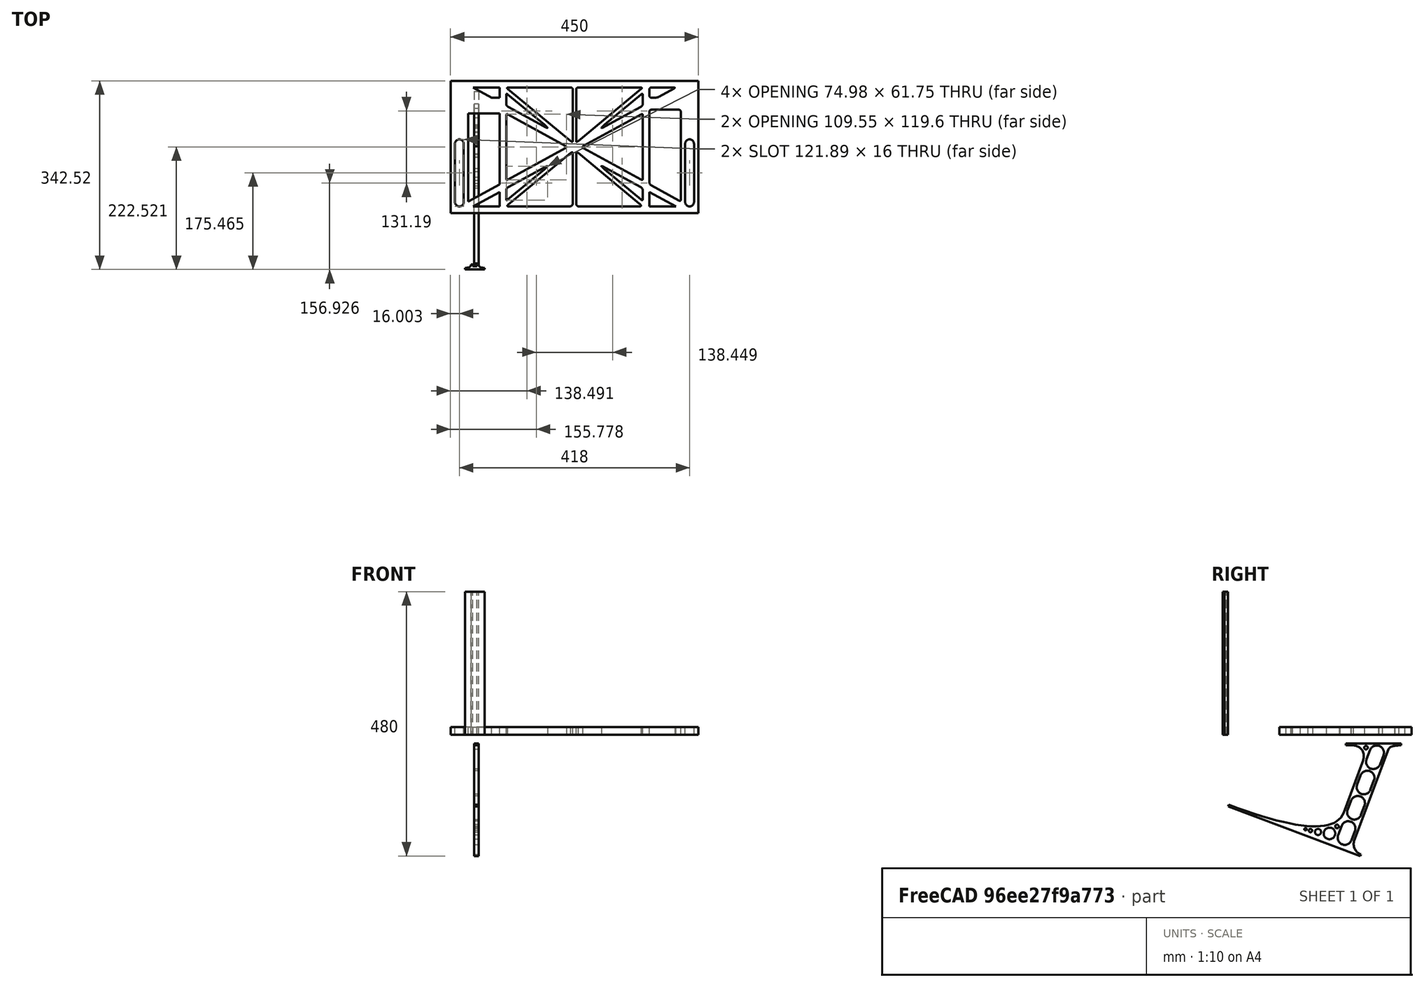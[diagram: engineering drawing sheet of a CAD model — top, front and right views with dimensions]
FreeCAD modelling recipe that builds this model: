
FCSTD DOCUMENT  (FreeCAD 0.19R0.19.2)
Label: laptopStand109
License: All rights reserved
LicenseURL: http://en.wikipedia.org/wiki/All_rights_reserved
objects: Sketcher::SketchObject×3, Part::Extrusion×3
note: 6 computed .brp shape members not serialized (recipe doc carries the construction recipe); baked Part::Feature solids carry a one-line shape summary decoded from their .brp

FEATURE [Sketcher::SketchObject] Sketch
  FullyConstrained = false
  sketch-geometry (298):
    g0: LineSegment StartX=-10.9272 StartY=-82.7794 StartZ=0 EndX=46.0728 EndY=-51.4823 EndZ=0
    g1: LineSegment StartX=366.073 StartY=-91.7794 StartZ=0 EndX=318.073 EndY=-65.424 EndZ=0
    g2: LineSegment StartX=-10.9272 StartY=77.3346 StartZ=0 EndX=-10.9272 EndY=-82.7794 EndZ=0
    g3: LineSegment StartX=-1.92719 StartY=-91.7794 StartZ=0 EndX=46.0728 EndY=-91.7794 EndZ=0
    g4: LineSegment StartX=318.073 StartY=-65.424 StartZ=0 EndX=318.073 EndY=-91.7794 EndZ=0
    g5: LineSegment StartX=318.073 StartY=-91.7794 StartZ=0 EndX=366.073 EndY=-91.7794 EndZ=0
    g6: LineSegment StartX=46.0728 StartY=-65.424 StartZ=0 EndX=-1.92719 EndY=-91.7794 EndZ=0
    g7: LineSegment StartX=46.0728 StartY=-65.424 StartZ=0 EndX=46.0728 EndY=-91.7794 EndZ=0
    g8: LineSegment StartX=46.0728 StartY=77.3346 StartZ=0 EndX=46.0728 EndY=-51.4823 EndZ=0
    g9: LineSegment StartX=-42.9272 StartY=136.221 StartZ=0 EndX=-42.9272 EndY=-103.779 EndZ=0
    g10: LineSegment StartX=407.073 StartY=136.221 StartZ=0 EndX=407.073 EndY=-103.779 EndZ=0
    g11: ArcOfCircle CenterX=-26.9272 CenterY=22.1087 CenterZ=0 NormalX=0 NormalY=0 NormalZ=1 AngleXU=0 Radius=8 StartAngle=1e-16 EndAngle=3.14159
    g12: ArcOfCircle CenterX=-26.9272 CenterY=-83.7794 CenterZ=0 NormalX=0 NormalY=0 NormalZ=1 AngleXU=0 Radius=8 StartAngle=3.14159 EndAngle=6.28319
    g13: LineSegment StartX=-34.9272 StartY=22.1087 StartZ=0 EndX=-34.9272 EndY=-83.7794 EndZ=0
    g14: LineSegment StartX=-18.9272 StartY=22.1087 StartZ=0 EndX=-18.9272 EndY=-83.7794 EndZ=0
    g15: ArcOfCircle CenterX=391.073 CenterY=22.1087 CenterZ=0 NormalX=0 NormalY=0 NormalZ=1 AngleXU=0 Radius=8 StartAngle=-4.4e-15 EndAngle=3.14159
    g16: LineSegment StartX=399.073 StartY=22.1087 StartZ=0 EndX=399.073 EndY=-83.7794 EndZ=0
    g17: LineSegment StartX=383.073 StartY=22.1087 StartZ=0 EndX=383.073 EndY=-83.7794 EndZ=0
    g18: ArcOfCircle CenterX=391.073 CenterY=-83.7794 CenterZ=0 NormalX=0 NormalY=0 NormalZ=1 AngleXU=0 Radius=8 StartAngle=3.14159 EndAngle=6.28319
    g19: Circle CenterX=175.022 CenterY=27.0628 CenterZ=0 NormalX=0 NormalY=0 NormalZ=1 AngleXU=0 Radius=1
    g20: Circle CenterX=179.022 CenterY=24.8665 CenterZ=0 NormalX=0 NormalY=0 NormalZ=1 AngleXU=0 Radius=1
    g21: Circle CenterX=179.022 CenterY=27.0628 CenterZ=0 NormalX=0 NormalY=0 NormalZ=1 AngleXU=0 Radius=1
    g22: BSplineCurve PolesCount=3 KnotsCount=2 Degree=2 IsPeriodic=0
    g23: GeomPoint X=175.022 Y=27.0628 Z=0
    g24: GeomPoint X=179.022 Y=27.0628 Z=0
    g25: Circle CenterX=189.124 CenterY=27.0628 CenterZ=0 NormalX=0 NormalY=0 NormalZ=1 AngleXU=0 Radius=1
    g26: Circle CenterX=185.124 CenterY=24.8665 CenterZ=0 NormalX=0 NormalY=0 NormalZ=1 AngleXU=0 Radius=1
    g27: Circle CenterX=185.124 CenterY=27.0628 CenterZ=0 NormalX=0 NormalY=0 NormalZ=1 AngleXU=0 Radius=1
    g28: BSplineCurve PolesCount=3 KnotsCount=2 Degree=2 IsPeriodic=0
    g29: GeomPoint X=189.124 Y=27.0628 Z=0
    g30: GeomPoint X=185.124 Y=27.0628 Z=0
    g31: Circle CenterX=175.022 CenterY=5.37834 CenterZ=0 NormalX=0 NormalY=0 NormalZ=1 AngleXU=0 Radius=1
    g32: Circle CenterX=179.022 CenterY=7.57463 CenterZ=0 NormalX=0 NormalY=0 NormalZ=1 AngleXU=0 Radius=1
    g33: Circle CenterX=179.022 CenterY=5.34704 CenterZ=0 NormalX=0 NormalY=0 NormalZ=1 AngleXU=0 Radius=1
    g34: BSplineCurve PolesCount=3 KnotsCount=2 Degree=2 IsPeriodic=0
    g35: GeomPoint X=175.022 Y=5.37834 Z=0
    g36: GeomPoint X=179.022 Y=5.34704 Z=0
    g37: Circle CenterX=189.124 CenterY=5.37834 CenterZ=0 NormalX=0 NormalY=0 NormalZ=1 AngleXU=0 Radius=1
    g38: Circle CenterX=185.124 CenterY=7.57463 CenterZ=0 NormalX=0 NormalY=0 NormalZ=1 AngleXU=0 Radius=1
    g39: Circle CenterX=185.124 CenterY=5.34704 CenterZ=0 NormalX=0 NormalY=0 NormalZ=1 AngleXU=0 Radius=1
    g40: BSplineCurve PolesCount=3 KnotsCount=2 Degree=2 IsPeriodic=0
    g41: GeomPoint X=189.124 Y=5.37834 Z=0
    g42: GeomPoint X=185.124 Y=5.34704 Z=0
    g43: Circle CenterX=165.871 CenterY=18.1458 CenterZ=0 NormalX=0 NormalY=0 NormalZ=1 AngleXU=0 Radius=1
    g44: Circle CenterX=169.377 CenterY=16.2206 CenterZ=0 NormalX=0 NormalY=0 NormalZ=1 AngleXU=0 Radius=1
    g45: Circle CenterX=165.871 CenterY=14.2954 CenterZ=0 NormalX=0 NormalY=0 NormalZ=1 AngleXU=0 Radius=1
    g46: BSplineCurve PolesCount=3 KnotsCount=2 Degree=2 IsPeriodic=0
    g47: GeomPoint X=165.871 Y=18.1458 Z=0
    g48: GeomPoint X=165.871 Y=14.2954 Z=0
    g49: Circle CenterX=198.275 CenterY=18.1458 CenterZ=0 NormalX=0 NormalY=0 NormalZ=1 AngleXU=0 Radius=1
    g50: Circle CenterX=194.768 CenterY=16.2206 CenterZ=0 NormalX=0 NormalY=0 NormalZ=1 AngleXU=0 Radius=1
    g51: Circle CenterX=198.275 CenterY=14.2954 CenterZ=0 NormalX=0 NormalY=0 NormalZ=1 AngleXU=0 Radius=1
    g52: BSplineCurve PolesCount=3 KnotsCount=2 Degree=2 IsPeriodic=0
    g53: GeomPoint X=198.275 Y=18.1458 Z=0
    g54: GeomPoint X=198.275 Y=14.2954 Z=0
    g55: LineSegment StartX=407.073 StartY=-103.779 StartZ=0 EndX=-42.9272 EndY=-103.779 EndZ=0
    g56: LineSegment StartX=407.073 StartY=136.221 StartZ=0 EndX=-42.9272 EndY=136.221 EndZ=0
    g57: LineSegment StartX=46.0728 StartY=77.3346 StartZ=0 EndX=-10.9272 EndY=77.3346 EndZ=0
    g58: LineSegment StartX=46.0728 StartY=105.865 StartZ=0 EndX=31.5028 EndY=105.865 EndZ=0
    g59: LineSegment StartX=46.0728 StartY=124.221 StartZ=0 EndX=46.0728 EndY=105.865 EndZ=0
    g60: LineSegment StartX=-1.92719 StartY=124.221 StartZ=0 EndX=31.5028 EndY=105.865 EndZ=0
    g61: LineSegment StartX=46.0728 StartY=124.221 StartZ=0 EndX=-1.92719 EndY=124.221 EndZ=0
    g62: Circle CenterX=125.607 CenterY=54.1951 CenterZ=0 NormalX=0 NormalY=0 NormalZ=1 AngleXU=0 Radius=1
    g63: Circle CenterX=139.632 CenterY=46.4944 CenterZ=0 NormalX=0 NormalY=0 NormalZ=1 AngleXU=0 Radius=1
    g64: Circle CenterX=127.326 CenterY=56.7187 CenterZ=0 NormalX=0 NormalY=0 NormalZ=1 AngleXU=0 Radius=1
    g65: BSplineCurve PolesCount=3 KnotsCount=2 Degree=2 IsPeriodic=0
    g66: GeomPoint X=125.607 Y=54.1951 Z=0
    g67: GeomPoint X=127.326 Y=56.7187 Z=0
    g68: Circle CenterX=236.821 CenterY=56.7187 CenterZ=0 NormalX=0 NormalY=0 NormalZ=1 AngleXU=0 Radius=1
    g69: Circle CenterX=224.513 CenterY=46.4944 CenterZ=0 NormalX=0 NormalY=0 NormalZ=1 AngleXU=0 Radius=1
    g70: Circle CenterX=238.538 CenterY=54.1951 CenterZ=0 NormalX=0 NormalY=0 NormalZ=1 AngleXU=0 Radius=1
    g71: BSplineCurve PolesCount=3 KnotsCount=2 Degree=2 IsPeriodic=0
    g72: GeomPoint X=236.821 Y=56.7187 Z=0
    g73: GeomPoint X=238.538 Y=54.1951 Z=0
    g74: Circle CenterX=238.538 CenterY=-21.7539 CenterZ=0 NormalX=0 NormalY=0 NormalZ=1 AngleXU=0 Radius=1
    g75: Circle CenterX=224.513 CenterY=-14.0532 CenterZ=0 NormalX=0 NormalY=0 NormalZ=1 AngleXU=0 Radius=1
    g76: Circle CenterX=236.821 CenterY=-24.2775 CenterZ=0 NormalX=0 NormalY=0 NormalZ=1 AngleXU=0 Radius=1
    g77: BSplineCurve PolesCount=3 KnotsCount=2 Degree=2 IsPeriodic=0
    g78: GeomPoint X=238.538 Y=-21.7539 Z=0
    g79: GeomPoint X=236.821 Y=-24.2775 Z=0
    g80: Circle CenterX=125.607 CenterY=-21.7539 CenterZ=0 NormalX=0 NormalY=0 NormalZ=1 AngleXU=0 Radius=1
    g81: Circle CenterX=139.632 CenterY=-14.0532 CenterZ=0 NormalX=0 NormalY=0 NormalZ=1 AngleXU=0 Radius=1
    g82: Circle CenterX=127.325 CenterY=-24.2775 CenterZ=0 NormalX=0 NormalY=0 NormalZ=1 AngleXU=0 Radius=1
    g83: BSplineCurve PolesCount=3 KnotsCount=2 Degree=2 IsPeriodic=0
    g84: GeomPoint X=125.607 Y=-21.7539 Z=0
    g85: GeomPoint X=127.325 Y=-24.2775 Z=0
    g86: Circle CenterX=302.996 CenterY=111.695 CenterZ=0 NormalX=0 NormalY=0 NormalZ=1 AngleXU=0 Radius=1
    g87: Circle CenterX=306.073 CenterY=114.251 CenterZ=0 NormalX=0 NormalY=0 NormalZ=1 AngleXU=0 Radius=1
    g88: Circle CenterX=306.073 CenterY=110.251 CenterZ=0 NormalX=0 NormalY=0 NormalZ=1 AngleXU=0 Radius=1
    g89: BSplineCurve PolesCount=3 KnotsCount=2 Degree=2 IsPeriodic=0
    g90: GeomPoint X=302.996 Y=111.695 Z=0
    g91: GeomPoint X=306.073 Y=110.251 Z=0
    g92: Circle CenterX=306.073 CenterY=95.2763 CenterZ=0 NormalX=0 NormalY=0 NormalZ=1 AngleXU=0 Radius=1
    g93: Circle CenterX=306.073 CenterY=91.2763 CenterZ=0 NormalX=0 NormalY=0 NormalZ=1 AngleXU=0 Radius=1
    g94: Circle CenterX=302.567 CenterY=89.3511 CenterZ=0 NormalX=0 NormalY=0 NormalZ=1 AngleXU=0 Radius=1
    g95: BSplineCurve PolesCount=3 KnotsCount=2 Degree=2 IsPeriodic=0
    g96: GeomPoint X=306.073 Y=95.2763 Z=0
    g97: GeomPoint X=302.567 Y=89.3511 Z=0
    g98: LineSegment StartX=306.073 StartY=110.251 StartZ=0 EndX=306.073 EndY=95.2763 EndZ=0
    g99: LineSegment StartX=302.996 StartY=111.695 StartZ=0 EndX=236.821 EndY=56.7187 EndZ=0
    g100: LineSegment StartX=238.538 StartY=54.1951 StartZ=0 EndX=302.567 EndY=89.3511 EndZ=0
    g101: Circle CenterX=61.1496 CenterY=111.695 CenterZ=0 NormalX=0 NormalY=0 NormalZ=1 AngleXU=0 Radius=1
    g102: Circle CenterX=58.0728 CenterY=114.251 CenterZ=0 NormalX=0 NormalY=0 NormalZ=1 AngleXU=0 Radius=1
    g103: Circle CenterX=58.0728 CenterY=110.251 CenterZ=0 NormalX=0 NormalY=0 NormalZ=1 AngleXU=0 Radius=1
    g104: BSplineCurve PolesCount=3 KnotsCount=2 Degree=2 IsPeriodic=0
    g105: GeomPoint X=61.1496 Y=111.695 Z=0
    g106: GeomPoint X=58.0728 Y=110.251 Z=0
    g107: Circle CenterX=61.5791 CenterY=89.3511 CenterZ=0 NormalX=0 NormalY=0 NormalZ=1 AngleXU=0 Radius=1
    g108: Circle CenterX=58.0728 CenterY=91.2763 CenterZ=0 NormalX=0 NormalY=0 NormalZ=1 AngleXU=0 Radius=1
    g109: Circle CenterX=58.0728 CenterY=95.2763 CenterZ=0 NormalX=0 NormalY=0 NormalZ=1 AngleXU=0 Radius=1
    g110: BSplineCurve PolesCount=3 KnotsCount=2 Degree=2 IsPeriodic=0
    g111: GeomPoint X=61.5791 Y=89.3511 Z=0
    g112: GeomPoint X=58.0728 Y=95.2763 Z=0
    g113: LineSegment StartX=58.0728 StartY=110.251 StartZ=0 EndX=58.0728 EndY=95.2763 EndZ=0
    g114: LineSegment StartX=61.1496 StartY=111.695 StartZ=0 EndX=127.326 EndY=56.7187 EndZ=0
    g115: LineSegment StartX=125.607 StartY=54.1951 StartZ=0 EndX=61.5791 EndY=89.3511 EndZ=0
    g116: Circle CenterX=61.5791 CenterY=-56.9099 CenterZ=0 NormalX=0 NormalY=0 NormalZ=1 AngleXU=0 Radius=1
    g117: Circle CenterX=58.0728 CenterY=-58.8351 CenterZ=0 NormalX=0 NormalY=0 NormalZ=1 AngleXU=0 Radius=1
    g118: Circle CenterX=58.0728 CenterY=-62.8351 CenterZ=0 NormalX=0 NormalY=0 NormalZ=1 AngleXU=0 Radius=1
    g119: BSplineCurve PolesCount=3 KnotsCount=2 Degree=2 IsPeriodic=0
    g120: GeomPoint X=61.5791 Y=-56.9099 Z=0
    g121: GeomPoint X=58.0728 Y=-62.8351 Z=0
    g122: Circle CenterX=58.0728 CenterY=-77.8102 CenterZ=0 NormalX=0 NormalY=0 NormalZ=1 AngleXU=0 Radius=1
    g123: Circle CenterX=58.0728 CenterY=-81.8102 CenterZ=0 NormalX=0 NormalY=0 NormalZ=1 AngleXU=0 Radius=1
    g124: Circle CenterX=61.1496 CenterY=-79.2541 CenterZ=0 NormalX=0 NormalY=0 NormalZ=1 AngleXU=0 Radius=1
    g125: BSplineCurve PolesCount=3 KnotsCount=2 Degree=2 IsPeriodic=0
    g126: GeomPoint X=58.0728 Y=-77.8102 Z=0
    g127: GeomPoint X=61.1496 Y=-79.2541 Z=0
    g128: LineSegment StartX=58.0728 StartY=-62.8351 StartZ=0 EndX=58.0728 EndY=-77.8102 EndZ=0
    g129: LineSegment StartX=61.1496 StartY=-79.2541 StartZ=0 EndX=127.325 EndY=-24.2775 EndZ=0
    g130: LineSegment StartX=125.607 StartY=-21.7539 StartZ=0 EndX=61.5791 EndY=-56.9099 EndZ=0
    g131: Circle CenterX=302.567 CenterY=-56.9099 CenterZ=0 NormalX=0 NormalY=0 NormalZ=1 AngleXU=0 Radius=1
    g132: Circle CenterX=306.073 CenterY=-58.8351 CenterZ=0 NormalX=0 NormalY=0 NormalZ=1 AngleXU=0 Radius=1
    g133: Circle CenterX=306.073 CenterY=-62.8351 CenterZ=0 NormalX=0 NormalY=0 NormalZ=1 AngleXU=0 Radius=1
    g134: BSplineCurve PolesCount=3 KnotsCount=2 Degree=2 IsPeriodic=0
    g135: GeomPoint X=302.567 Y=-56.9099 Z=0
    g136: GeomPoint X=306.073 Y=-62.8351 Z=0
    g137: Circle CenterX=302.996 CenterY=-79.2541 CenterZ=0 NormalX=0 NormalY=0 NormalZ=1 AngleXU=0 Radius=1
    g138: Circle CenterX=306.073 CenterY=-81.8102 CenterZ=0 NormalX=0 NormalY=0 NormalZ=1 AngleXU=0 Radius=1
    g139: Circle CenterX=306.073 CenterY=-77.8102 CenterZ=0 NormalX=0 NormalY=0 NormalZ=1 AngleXU=0 Radius=1
    g140: BSplineCurve PolesCount=3 KnotsCount=2 Degree=2 IsPeriodic=0
    g141: GeomPoint X=302.996 Y=-79.2541 Z=0
    g142: GeomPoint X=306.073 Y=-77.8102 Z=0
    g143: LineSegment StartX=306.073 StartY=-62.8351 StartZ=0 EndX=306.073 EndY=-77.8102 EndZ=0
    g144: LineSegment StartX=302.996 StartY=-79.2541 StartZ=0 EndX=236.821 EndY=-24.2775 EndZ=0
    g145: LineSegment StartX=238.538 StartY=-21.7539 StartZ=0 EndX=302.567 EndY=-56.9099 EndZ=0
    g146: Circle CenterX=61.6457 CenterY=-88.8112 CenterZ=0 NormalX=0 NormalY=0 NormalZ=1 AngleXU=0 Radius=1
    g147: Circle CenterX=58.0728 CenterY=-91.7794 CenterZ=0 NormalX=0 NormalY=0 NormalZ=1 AngleXU=0 Radius=1
    g148: Circle CenterX=63.9135 CenterY=-91.7794 CenterZ=0 NormalX=0 NormalY=0 NormalZ=1 AngleXU=0 Radius=1
    g149: BSplineCurve PolesCount=3 KnotsCount=2 Degree=2 IsPeriodic=0
    g150: GeomPoint X=61.6457 Y=-88.8112 Z=0
    g151: GeomPoint X=63.9135 Y=-91.7794 Z=0
    g152: Circle CenterX=179.022 CenterY=-85.8163 CenterZ=0 NormalX=0 NormalY=0 NormalZ=1 AngleXU=0 Radius=1
    g153: Circle CenterX=179.022 CenterY=-91.7794 CenterZ=0 NormalX=0 NormalY=0 NormalZ=1 AngleXU=0 Radius=1
    g154: Circle CenterX=171.895 CenterY=-91.7794 CenterZ=0 NormalX=0 NormalY=0 NormalZ=1 AngleXU=0 Radius=1
    g155: BSplineCurve PolesCount=3 KnotsCount=2 Degree=2 IsPeriodic=0
    g156: GeomPoint X=179.022 Y=-85.8163 Z=0
    g157: GeomPoint X=171.895 Y=-91.7794 Z=0
    g158: Circle CenterX=185.124 CenterY=-86.2028 CenterZ=0 NormalX=0 NormalY=0 NormalZ=1 AngleXU=0 Radius=1
    g159: Circle CenterX=185.124 CenterY=-91.7794 CenterZ=0 NormalX=0 NormalY=0 NormalZ=1 AngleXU=0 Radius=1
    g160: Circle CenterX=191.747 CenterY=-91.7794 CenterZ=0 NormalX=0 NormalY=0 NormalZ=1 AngleXU=0 Radius=1
    g161: BSplineCurve PolesCount=3 KnotsCount=2 Degree=2 IsPeriodic=0
    g162: GeomPoint X=185.124 Y=-86.2028 Z=0
    g163: GeomPoint X=191.747 Y=-91.7794 Z=0
    g164: Circle CenterX=299.888 CenterY=-86.6413 CenterZ=0 NormalX=0 NormalY=0 NormalZ=1 AngleXU=0 Radius=1
    g165: Circle CenterX=306.073 CenterY=-91.7794 CenterZ=0 NormalX=0 NormalY=0 NormalZ=1 AngleXU=0 Radius=1
    g166: Circle CenterX=298.776 CenterY=-91.7794 CenterZ=0 NormalX=0 NormalY=0 NormalZ=1 AngleXU=0 Radius=1
    g167: BSplineCurve PolesCount=3 KnotsCount=2 Degree=2 IsPeriodic=0
    g168: GeomPoint X=299.888 Y=-86.6413 Z=0
    g169: GeomPoint X=298.776 Y=-91.7794 Z=0
    g170: LineSegment StartX=189.124 StartY=5.37834 StartZ=0 EndX=299.888 EndY=-86.6413 EndZ=0
    g171: LineSegment StartX=298.776 StartY=-91.7794 StartZ=0 EndX=191.747 EndY=-91.7794 EndZ=0
    g172: LineSegment StartX=185.124 StartY=-86.2028 StartZ=0 EndX=185.124 EndY=5.34704 EndZ=0
    g173: LineSegment StartX=179.022 StartY=5.34704 StartZ=0 EndX=179.022 EndY=-85.8163 EndZ=0
    g174: LineSegment StartX=171.895 StartY=-91.7794 StartZ=0 EndX=63.9135 EndY=-91.7794 EndZ=0
    g175: LineSegment StartX=61.6457 StartY=-88.8112 StartZ=0 EndX=175.022 EndY=5.37834 EndZ=0
    g176: Circle CenterX=302.073 CenterY=124.221 CenterZ=0 NormalX=0 NormalY=0 NormalZ=1 AngleXU=0 Radius=1
    g177: Circle CenterX=306.073 CenterY=124.221 CenterZ=0 NormalX=0 NormalY=0 NormalZ=1 AngleXU=0 Radius=1
    g178: Circle CenterX=302.996 CenterY=121.665 CenterZ=0 NormalX=0 NormalY=0 NormalZ=1 AngleXU=0 Radius=1
    g179: BSplineCurve PolesCount=3 KnotsCount=2 Degree=2 IsPeriodic=0
    g180: GeomPoint X=302.073 Y=124.221 Z=0
    g181: GeomPoint X=302.996 Y=121.665 Z=0
    g182: Circle CenterX=189.124 CenterY=124.221 CenterZ=0 NormalX=0 NormalY=0 NormalZ=1 AngleXU=0 Radius=1
    g183: Circle CenterX=185.124 CenterY=124.221 CenterZ=0 NormalX=0 NormalY=0 NormalZ=1 AngleXU=0 Radius=1
    g184: Circle CenterX=185.124 CenterY=120.221 CenterZ=0 NormalX=0 NormalY=0 NormalZ=1 AngleXU=0 Radius=1
    g185: BSplineCurve PolesCount=3 KnotsCount=2 Degree=2 IsPeriodic=0
    g186: GeomPoint X=189.124 Y=124.221 Z=0
    g187: GeomPoint X=185.124 Y=120.221 Z=0
    g188: Circle CenterX=175.022 CenterY=124.221 CenterZ=0 NormalX=0 NormalY=0 NormalZ=1 AngleXU=0 Radius=1
    g189: Circle CenterX=179.022 CenterY=124.221 CenterZ=0 NormalX=0 NormalY=0 NormalZ=1 AngleXU=0 Radius=1
    g190: Circle CenterX=179.022 CenterY=120.221 CenterZ=0 NormalX=0 NormalY=0 NormalZ=1 AngleXU=0 Radius=1
    g191: BSplineCurve PolesCount=3 KnotsCount=2 Degree=2 IsPeriodic=0
    g192: GeomPoint X=175.022 Y=124.221 Z=0
    g193: GeomPoint X=179.022 Y=120.221 Z=0
    g194: Circle CenterX=62.0728 CenterY=124.221 CenterZ=0 NormalX=0 NormalY=0 NormalZ=1 AngleXU=0 Radius=1
    g195: Circle CenterX=58.0728 CenterY=124.221 CenterZ=0 NormalX=0 NormalY=0 NormalZ=1 AngleXU=0 Radius=1
    g196: Circle CenterX=61.1496 CenterY=121.665 CenterZ=0 NormalX=0 NormalY=0 NormalZ=1 AngleXU=0 Radius=1
    g197: BSplineCurve PolesCount=3 KnotsCount=2 Degree=2 IsPeriodic=0
    g198: GeomPoint X=62.0728 Y=124.221 Z=0
    g199: GeomPoint X=61.1496 Y=121.665 Z=0
    g200: LineSegment StartX=62.0728 StartY=124.221 StartZ=0 EndX=175.022 EndY=124.221 EndZ=0
    g201: LineSegment StartX=179.022 StartY=120.221 StartZ=0 EndX=179.022 EndY=27.0628 EndZ=0
    g202: LineSegment StartX=185.124 StartY=27.0628 StartZ=0 EndX=185.124 EndY=120.221 EndZ=0
    g203: LineSegment StartX=189.124 StartY=124.221 StartZ=0 EndX=302.073 EndY=124.221 EndZ=0
    g204: LineSegment StartX=302.996 StartY=121.665 StartZ=0 EndX=189.124 EndY=27.0628 EndZ=0
    g205: LineSegment StartX=175.022 StartY=27.0628 StartZ=0 EndX=61.1496 EndY=121.665 EndZ=0
    g206: Circle CenterX=61.5791 CenterY=75.4095 CenterZ=0 NormalX=0 NormalY=0 NormalZ=1 AngleXU=0 Radius=1
    g207: Circle CenterX=58.0728 CenterY=77.3346 CenterZ=0 NormalX=0 NormalY=0 NormalZ=1 AngleXU=0 Radius=1
    g208: Circle CenterX=58.0728 CenterY=73.3346 CenterZ=0 NormalX=0 NormalY=0 NormalZ=1 AngleXU=0 Radius=1
    g209: BSplineCurve PolesCount=3 KnotsCount=2 Degree=2 IsPeriodic=0
    g210: GeomPoint X=61.5791 Y=75.4095 Z=0
    g211: GeomPoint X=58.0728 Y=73.3346 Z=0
    g212: Circle CenterX=58.0728 CenterY=-40.8935 CenterZ=0 NormalX=0 NormalY=0 NormalZ=1 AngleXU=0 Radius=1
    g213: Circle CenterX=58.0728 CenterY=-44.8935 CenterZ=0 NormalX=0 NormalY=0 NormalZ=1 AngleXU=0 Radius=1
    g214: Circle CenterX=61.5791 CenterY=-42.9683 CenterZ=0 NormalX=0 NormalY=0 NormalZ=1 AngleXU=0 Radius=1
    g215: BSplineCurve PolesCount=3 KnotsCount=2 Degree=2 IsPeriodic=0
    g216: GeomPoint X=58.0728 Y=-40.8935 Z=0
    g217: GeomPoint X=61.5791 Y=-42.9683 Z=0
    g218: LineSegment StartX=61.5791 StartY=-42.9683 StartZ=0 EndX=165.871 EndY=14.2954 EndZ=0
    g219: LineSegment StartX=165.871 StartY=18.1458 StartZ=0 EndX=61.5791 EndY=75.4095 EndZ=0
    g220: LineSegment StartX=58.0728 StartY=73.3346 StartZ=0 EndX=58.0728 EndY=-40.8935 EndZ=0
    g221: Circle CenterX=302.567 CenterY=-42.9683 CenterZ=0 NormalX=0 NormalY=0 NormalZ=1 AngleXU=0 Radius=1
    g222: Circle CenterX=306.073 CenterY=-44.8935 CenterZ=0 NormalX=0 NormalY=0 NormalZ=1 AngleXU=0 Radius=1
    g223: Circle CenterX=306.073 CenterY=-40.8935 CenterZ=0 NormalX=0 NormalY=0 NormalZ=1 AngleXU=0 Radius=1
    g224: BSplineCurve PolesCount=3 KnotsCount=2 Degree=2 IsPeriodic=0
    g225: GeomPoint X=302.567 Y=-42.9683 Z=0
    g226: GeomPoint X=306.073 Y=-40.8935 Z=0
    g227: Circle CenterX=306.073 CenterY=73.3346 CenterZ=0 NormalX=0 NormalY=0 NormalZ=1 AngleXU=0 Radius=1
    g228: Circle CenterX=306.073 CenterY=77.3346 CenterZ=0 NormalX=0 NormalY=0 NormalZ=1 AngleXU=0 Radius=1
    g229: Circle CenterX=302.567 CenterY=75.4095 CenterZ=0 NormalX=0 NormalY=0 NormalZ=1 AngleXU=0 Radius=1
    g230: BSplineCurve PolesCount=3 KnotsCount=2 Degree=2 IsPeriodic=0
    g231: GeomPoint X=306.073 Y=73.3346 Z=0
    g232: GeomPoint X=302.567 Y=75.4095 Z=0
    g233: LineSegment StartX=302.567 StartY=-42.9683 StartZ=0 EndX=198.275 EndY=14.2954 EndZ=0
    g234: LineSegment StartX=198.275 StartY=18.1458 StartZ=0 EndX=302.567 EndY=75.4095 EndZ=0
    g235: LineSegment StartX=306.073 StartY=73.3346 StartZ=0 EndX=306.073 EndY=-40.8935 EndZ=0
    g236: LineSegment StartX=322.073 StartY=105.865 StartZ=0 EndX=328.643 EndY=105.865 EndZ=0
    g237: LineSegment StartX=318.073 StartY=120.221 StartZ=0 EndX=318.073 EndY=109.865 EndZ=0
    g238: LineSegment StartX=336.157 StartY=107.779 StartZ=0 EndX=362.567 EndY=122.294 EndZ=0
    g239: Circle CenterX=362.073 CenterY=124.221 CenterZ=0 NormalX=0 NormalY=0 NormalZ=1 AngleXU=0 Radius=1
    g240: Circle CenterX=366.073 CenterY=124.221 CenterZ=0 NormalX=0 NormalY=0 NormalZ=1 AngleXU=0 Radius=1
    g241: Circle CenterX=362.567 CenterY=122.294 CenterZ=0 NormalX=0 NormalY=0 NormalZ=1 AngleXU=0 Radius=1
    g242: BSplineCurve PolesCount=3 KnotsCount=2 Degree=2 IsPeriodic=0
    g243: GeomPoint X=362.073 Y=124.221 Z=0
    g244: GeomPoint X=362.567 Y=122.294 Z=0
    g245: Circle CenterX=322.073 CenterY=124.221 CenterZ=0 NormalX=0 NormalY=0 NormalZ=1 AngleXU=0 Radius=1
    g246: Circle CenterX=318.073 CenterY=124.221 CenterZ=0 NormalX=0 NormalY=0 NormalZ=1 AngleXU=0 Radius=1
    g247: Circle CenterX=318.073 CenterY=120.221 CenterZ=0 NormalX=0 NormalY=0 NormalZ=1 AngleXU=0 Radius=1
    g248: BSplineCurve PolesCount=3 KnotsCount=2 Degree=2 IsPeriodic=0
    g249: GeomPoint X=322.073 Y=124.221 Z=0
    g250: GeomPoint X=318.073 Y=120.221 Z=0
    g251: Circle CenterX=322.073 CenterY=105.865 CenterZ=0 NormalX=0 NormalY=0 NormalZ=1 AngleXU=0 Radius=1
    g252: Circle CenterX=318.073 CenterY=105.865 CenterZ=0 NormalX=0 NormalY=0 NormalZ=1 AngleXU=0 Radius=1
    g253: Circle CenterX=318.073 CenterY=109.865 CenterZ=0 NormalX=0 NormalY=0 NormalZ=1 AngleXU=0 Radius=1
    g254: BSplineCurve PolesCount=3 KnotsCount=2 Degree=2 IsPeriodic=0
    g255: GeomPoint X=322.073 Y=105.865 Z=0
    g256: GeomPoint X=318.073 Y=109.865 Z=0
    g257: Circle CenterX=336.157 CenterY=107.779 CenterZ=0 NormalX=0 NormalY=0 NormalZ=1 AngleXU=0 Radius=1
    g258: Circle CenterX=332.651 CenterY=105.853 CenterZ=0 NormalX=0 NormalY=0 NormalZ=1 AngleXU=0 Radius=1
    g259: Circle CenterX=328.643 CenterY=105.865 CenterZ=0 NormalX=0 NormalY=0 NormalZ=1 AngleXU=0 Radius=1
    g260: BSplineCurve PolesCount=3 KnotsCount=2 Degree=2 IsPeriodic=0
    g261: GeomPoint X=336.157 Y=107.779 Z=0
    g262: GeomPoint X=328.643 Y=105.865 Z=0
    g263: LineSegment StartX=322.073 StartY=124.221 StartZ=0 EndX=362.073 EndY=124.221 EndZ=0
    g264: Circle CenterX=371.567 CenterY=-80.8644 CenterZ=0 NormalX=0 NormalY=0 NormalZ=1 AngleXU=0 Radius=1
    g265: Circle CenterX=375.073 CenterY=-82.7896 CenterZ=0 NormalX=0 NormalY=0 NormalZ=1 AngleXU=0 Radius=1
    g266: Circle CenterX=375.073 CenterY=-78.7896 CenterZ=0 NormalX=0 NormalY=0 NormalZ=1 AngleXU=0 Radius=1
    g267: BSplineCurve PolesCount=3 KnotsCount=2 Degree=2 IsPeriodic=0
    g268: GeomPoint X=371.567 Y=-80.8644 Z=0
    g269: GeomPoint X=375.073 Y=-78.7896 Z=0
    g270: Circle CenterX=321.579 CenterY=-53.4075 CenterZ=0 NormalX=0 NormalY=0 NormalZ=1 AngleXU=0 Radius=1
    g271: Circle CenterX=318.073 CenterY=-51.4823 CenterZ=0 NormalX=0 NormalY=0 NormalZ=1 AngleXU=0 Radius=1
    g272: Circle CenterX=318.073 CenterY=-47.4823 CenterZ=0 NormalX=0 NormalY=0 NormalZ=1 AngleXU=0 Radius=1
    g273: BSplineCurve PolesCount=3 KnotsCount=2 Degree=2 IsPeriodic=0
    g274: GeomPoint X=321.579 Y=-53.4075 Z=0
    g275: GeomPoint X=318.073 Y=-47.4823 Z=0
    g276: Circle CenterX=318.073 CenterY=79.9235 CenterZ=0 NormalX=0 NormalY=0 NormalZ=1 AngleXU=0 Radius=1
    g277: Circle CenterX=318.073 CenterY=83.9235 CenterZ=0 NormalX=0 NormalY=0 NormalZ=1 AngleXU=0 Radius=1
    g278: Circle CenterX=322.073 CenterY=83.9235 CenterZ=0 NormalX=0 NormalY=0 NormalZ=1 AngleXU=0 Radius=1
    g279: BSplineCurve PolesCount=3 KnotsCount=2 Degree=2 IsPeriodic=0
    g280: GeomPoint X=318.073 Y=79.9235 Z=0
    g281: GeomPoint X=322.073 Y=83.9235 Z=0
    g282: Circle CenterX=375.073 CenterY=79.9235 CenterZ=0 NormalX=0 NormalY=0 NormalZ=1 AngleXU=0 Radius=1
    g283: Circle CenterX=375.073 CenterY=83.9235 CenterZ=0 NormalX=0 NormalY=0 NormalZ=1 AngleXU=0 Radius=1
    g284: Circle CenterX=371.073 CenterY=83.9235 CenterZ=0 NormalX=0 NormalY=0 NormalZ=1 AngleXU=0 Radius=1
    g285: BSplineCurve PolesCount=3 KnotsCount=2 Degree=2 IsPeriodic=0
    g286: GeomPoint X=375.073 Y=79.9235 Z=0
    g287: GeomPoint X=371.073 Y=83.9235 Z=0
    g288: LineSegment StartX=322.073 StartY=83.9235 StartZ=0 EndX=371.073 EndY=83.9235 EndZ=0
    g289: LineSegment StartX=375.073 StartY=79.9235 StartZ=0 EndX=375.073 EndY=-78.7896 EndZ=0
    g290: LineSegment StartX=371.567 StartY=-80.8644 StartZ=0 EndX=321.579 EndY=-53.4075 EndZ=0
    g291: LineSegment StartX=318.073 StartY=-47.4823 StartZ=0 EndX=318.073 EndY=79.9235 EndZ=0
    g292: LineSegment StartX=320.347 StartY=-65.5714 StartZ=0 EndX=323.853 EndY=-67.4966 EndZ=0
    g293: LineSegment StartX=365.272 StartY=-90.3095 StartZ=0 EndX=361.765 EndY=-88.3843 EndZ=0
    g294: LineSegment StartX=363.279 StartY=-92.7205 StartZ=0 EndX=359.279 EndY=-92.7205 EndZ=0
    g295: LineSegment StartX=320.798 StartY=-92.6854 StartZ=0 EndX=324.798 EndY=-92.6854 EndZ=0
    g296: LineSegment StartX=317.038 StartY=-91.3099 StartZ=0 EndX=317.038 EndY=-87.3099 EndZ=0
    g297: LineSegment StartX=317.566 StartY=-65.567 StartZ=0 EndX=317.566 EndY=-69.567 EndZ=0
  constraints (500):
    c: Horizontal(g3)
    c: Coincident(g4,g1)
    c: Coincident(g7,g6)
    c: Coincident(g0,g8)
    c: Block(g1)
    c: Block(g4)
    c: Block(g7)
    c: Block(g6)
    c: Block(g0)
    c: Block(g2)
    c: Block(g5)
    c: Block(g3)
    c: Vertical(g9)
    c: Vertical(g10)
    c: Block(g10)
    c: Block(g9)
    c: Tangent(g11,g14) = 1.5708
    c: Tangent(g11,g13) = -1.5708
    c: Tangent(g13,g12) = -1.5708
    c: Tangent(g14,g12) = 1.5708
    c: Vertical(g13)
    c: Equal(g11,g12)
    c: Block(g14)
    c: Block(g13)
    c: Tangent(g15,g16) = 1.5708
    c: Tangent(g16,g18) = 1.5708
    c: Equal(g15,g18)
    c: Coincident(g17,g15)
    c: Coincident(g17,g18)
    c: Block(g16)
    c: Block(g17)
    c: Weight(g19) = 1
    c: Equal(g19,g20)
    c: Equal(g19,g21)
    c: InternalAlignment(g19,g22)
    c: InternalAlignment(g20,g22)
    c: InternalAlignment(g21,g22)
    c: InternalAlignment(g23,g22)
    c: InternalAlignment(g24,g22)
    c: Weight(g25) = 1
    c: Equal(g25,g26)
    c: Equal(g25,g27)
    c: InternalAlignment(g25,g28)
    c: InternalAlignment(g26,g28)
    c: InternalAlignment(g27,g28)
    c: InternalAlignment(g29,g28)
    c: InternalAlignment(g30,g28)
    c: Block(g28)
    c: Block(g22)
    c: Weight(g31) = 1
    c: Equal(g31,g32)
    c: Equal(g31,g33)
    c: InternalAlignment(g31,g34)
    c: InternalAlignment(g32,g34)
    c: InternalAlignment(g33,g34)
    c: InternalAlignment(g35,g34)
    c: InternalAlignment(g36,g34)
    c: Weight(g37) = 1
    c: Equal(g37,g38)
    c: Equal(g37,g39)
    c: InternalAlignment(g37,g40)
    c: InternalAlignment(g38,g40)
    c: InternalAlignment(g39,g40)
    c: InternalAlignment(g41,g40)
    c: InternalAlignment(g42,g40)
    c: Block(g40)
    c: Block(g34)
    c: Weight(g43) = 1
    c: Equal(g43,g44)
    c: Equal(g43,g45)
    c: InternalAlignment(g43,g46)
    c: InternalAlignment(g44,g46)
    c: InternalAlignment(g45,g46)
    c: InternalAlignment(g47,g46)
    c: InternalAlignment(g48,g46)
    c: Weight(g49) = 1
    c: Equal(g49,g50)
    c: Equal(g49,g51)
    c: InternalAlignment(g49,g52)
    c: InternalAlignment(g50,g52)
    c: InternalAlignment(g51,g52)
    c: InternalAlignment(g53,g52)
    c: InternalAlignment(g54,g52)
    c: Block(g46)
    c: Block(g52)
    c: Coincident(g55,g10)
    c: Coincident(g55,g9)
    c: Horizontal(g55)
    c: Distance(g55) = 450
    c: Coincident(g56,g10)
    c: Coincident(g56,g9)
    c: Horizontal(g56)
    c: Horizontal(g57)
    c: Coincident(g8,g57)
    c: Horizontal(g58)
    c: Vertical(g59)
    c: Block(g59)
    c: Block(g58)
    c: Block(g57)
    c: Distance(g59) = 18.3554
    c: Coincident(g61,g59)
    c: Coincident(g61,g60)
    c: Horizontal(g61)
    c: Block(g61)
    c: Block(g60)
    c: Coincident(g58,g60)
    c: Coincident(g2,g57)
    c: Weight(g62) = 1
    c: Equal(g62,g63)
    c: Equal(g62,g64)
    c: InternalAlignment(g62,g65)
    c: InternalAlignment(g63,g65)
    c: InternalAlignment(g64,g65)
    c: InternalAlignment(g66,g65)
    c: InternalAlignment(g67,g65)
    c: Block(g65)
    c: Weight(g68) = 1
    c: Equal(g68,g69)
    c: Equal(g68,g70)
    c: InternalAlignment(g68,g71)
    c: InternalAlignment(g69,g71)
    c: InternalAlignment(g70,g71)
    c: InternalAlignment(g72,g71)
    c: InternalAlignment(g73,g71)
    c: Block(g71)
    c: Weight(g74) = 1
    c: Equal(g74,g75)
    c: Equal(g74,g76)
    c: InternalAlignment(g74,g77)
    c: InternalAlignment(g75,g77)
    c: InternalAlignment(g76,g77)
    c: InternalAlignment(g78,g77)
    c: InternalAlignment(g79,g77)
    c: Block(g77)
    c: Weight(g80) = 1
    c: Equal(g80,g81)
    c: Equal(g80,g82)
    c: InternalAlignment(g80,g83)
    c: InternalAlignment(g81,g83)
    c: InternalAlignment(g82,g83)
    c: InternalAlignment(g84,g83)
    c: InternalAlignment(g85,g83)
    c: Block(g83)
    c: Weight(g86) = 1
    c: Equal(g86,g87)
    c: Equal(g86,g88)
    c: InternalAlignment(g86,g89)
    c: InternalAlignment(g87,g89)
    c: InternalAlignment(g88,g89)
    c: InternalAlignment(g90,g89)
    c: InternalAlignment(g91,g89)
    c: Weight(g92) = 1
    c: Equal(g92,g93)
    c: Equal(g92,g94)
    c: InternalAlignment(g92,g95)
    c: InternalAlignment(g93,g95)
    c: InternalAlignment(g94,g95)
    c: InternalAlignment(g96,g95)
    c: InternalAlignment(g97,g95)
    c: Block(g89)
    c: Block(g95)
    c: Coincident(g98,g89)
    c: Coincident(g98,g95)
    c: Vertical(g98)
    c: Coincident(g99,g89)
    c: Coincident(g99,g71)
    c: Coincident(g100,g71)
    c: Coincident(g100,g95)
    c: Weight(g101) = 1
    c: Equal(g101,g102)
    c: Equal(g101,g103)
    c: InternalAlignment(g101,g104)
    c: InternalAlignment(g102,g104)
    c: InternalAlignment(g103,g104)
    c: InternalAlignment(g105,g104)
    c: InternalAlignment(g106,g104)
    c: Weight(g107) = 1
    c: Equal(g107,g108)
    c: Equal(g107,g109)
    c: InternalAlignment(g107,g110)
    c: InternalAlignment(g108,g110)
    c: InternalAlignment(g109,g110)
    c: InternalAlignment(g111,g110)
    c: InternalAlignment(g112,g110)
    c: Block(g104)
    c: Block(g110)
    c: Coincident(g113,g104)
    c: Coincident(g113,g110)
    c: Vertical(g113)
    c: Coincident(g114,g104)
    c: Coincident(g114,g65)
    c: Coincident(g115,g65)
    c: Coincident(g115,g110)
    c: Weight(g116) = 1
    c: Equal(g116,g117)
    c: Equal(g116,g118)
    c: InternalAlignment(g116,g119)
    c: InternalAlignment(g117,g119)
    c: InternalAlignment(g118,g119)
    c: InternalAlignment(g120,g119)
    c: InternalAlignment(g121,g119)
    c: Weight(g122) = 1
    c: Equal(g122,g123)
    c: Equal(g122,g124)
    c: InternalAlignment(g122,g125)
    c: InternalAlignment(g123,g125)
    c: InternalAlignment(g124,g125)
    c: InternalAlignment(g126,g125)
    c: InternalAlignment(g127,g125)
    c: Block(g119)
    c: Block(g125)
    c: Coincident(g128,g119)
    c: Coincident(g128,g125)
    c: Vertical(g128)
    c: Coincident(g129,g125)
    c: Coincident(g129,g83)
    c: Coincident(g130,g83)
    c: Coincident(g130,g119)
    c: Weight(g131) = 1
    c: Equal(g131,g132)
    c: Equal(g131,g133)
    c: InternalAlignment(g131,g134)
    c: InternalAlignment(g132,g134)
    c: InternalAlignment(g133,g134)
    c: InternalAlignment(g135,g134)
    c: InternalAlignment(g136,g134)
    c: Weight(g137) = 1
    c: Equal(g137,g138)
    c: Equal(g137,g139)
    c: InternalAlignment(g137,g140)
    c: InternalAlignment(g138,g140)
    c: InternalAlignment(g139,g140)
    c: InternalAlignment(g141,g140)
    c: InternalAlignment(g142,g140)
    c: Block(g134)
    c: Block(g140)
    c: Coincident(g143,g134)
    c: Coincident(g143,g140)
    c: Vertical(g143)
    c: Coincident(g144,g140)
    c: Coincident(g144,g77)
    c: Coincident(g145,g77)
    c: Coincident(g145,g134)
    c: Weight(g146) = 1
    c: Equal(g146,g147)
    c: Equal(g146,g148)
    c: InternalAlignment(g146,g149)
    c: InternalAlignment(g147,g149)
    c: InternalAlignment(g148,g149)
    c: InternalAlignment(g150,g149)
    c: InternalAlignment(g151,g149)
    c: Weight(g152) = 1
    c: Equal(g152,g153)
    c: Equal(g152,g154)
    c: InternalAlignment(g152,g155)
    c: InternalAlignment(g153,g155)
    c: InternalAlignment(g154,g155)
    c: InternalAlignment(g156,g155)
    c: InternalAlignment(g157,g155)
    c: Weight(g158) = 1
    c: Equal(g158,g159)
    c: Equal(g158,g160)
    c: InternalAlignment(g158,g161)
    c: InternalAlignment(g159,g161)
    c: InternalAlignment(g160,g161)
    c: InternalAlignment(g162,g161)
    c: InternalAlignment(g163,g161)
    c: Weight(g164) = 1
    c: Equal(g164,g165)
    c: Equal(g164,g166)
    c: InternalAlignment(g164,g167)
    c: InternalAlignment(g165,g167)
    c: InternalAlignment(g166,g167)
    c: InternalAlignment(g168,g167)
    c: InternalAlignment(g169,g167)
    c: Block(g167)
    c: Block(g161)
    c: Block(g155)
    c: Block(g149)
    c: Coincident(g170,g40)
    c: Coincident(g170,g167)
    c: Coincident(g171,g167)
    c: Coincident(g171,g161)
    c: Horizontal(g171)
    c: Coincident(g172,g161)
    c: Coincident(g172,g40)
    c: Vertical(g172)
    c: Coincident(g173,g34)
    c: Coincident(g173,g155)
    c: Vertical(g173)
    c: Coincident(g174,g155)
    c: Coincident(g174,g149)
    c: Horizontal(g174)
    c: Coincident(g175,g149)
    c: Coincident(g175,g34)
    c: Weight(g176) = 1
    c: Equal(g176,g177)
    c: Equal(g176,g178)
    c: InternalAlignment(g176,g179)
    c: InternalAlignment(g177,g179)
    c: InternalAlignment(g178,g179)
    c: InternalAlignment(g180,g179)
    c: InternalAlignment(g181,g179)
    c: Weight(g182) = 1
    c: Equal(g182,g183)
    c: Equal(g182,g184)
    c: InternalAlignment(g182,g185)
    c: InternalAlignment(g183,g185)
    c: InternalAlignment(g184,g185)
    c: InternalAlignment(g186,g185)
    c: InternalAlignment(g187,g185)
    c: Weight(g188) = 1
    c: Equal(g188,g189)
    c: Equal(g188,g190)
    c: InternalAlignment(g188,g191)
    c: InternalAlignment(g189,g191)
    c: InternalAlignment(g190,g191)
    c: InternalAlignment(g192,g191)
    c: InternalAlignment(g193,g191)
    c: Weight(g194) = 1
    c: Equal(g194,g195)
    c: Equal(g194,g196)
    c: InternalAlignment(g194,g197)
    c: InternalAlignment(g195,g197)
    c: InternalAlignment(g196,g197)
    c: InternalAlignment(g198,g197)
    c: InternalAlignment(g199,g197)
    c: Block(g197)
    c: Block(g191)
    c: Block(g185)
    c: Block(g179)
    c: Coincident(g200,g197)
    c: Coincident(g200,g191)
    c: Horizontal(g200)
    c: Coincident(g201,g191)
    c: Coincident(g201,g22)
    c: Vertical(g201)
    c: Coincident(g202,g28)
    c: Coincident(g202,g185)
    c: Vertical(g202)
    c: Coincident(g203,g185)
    c: Coincident(g203,g179)
    c: Horizontal(g203)
    c: Coincident(g204,g179)
    c: Coincident(g204,g28)
    c: Coincident(g205,g22)
    c: Weight(g206) = 1
    c: Equal(g206,g207)
    c: Equal(g206,g208)
    c: InternalAlignment(g206,g209)
    c: InternalAlignment(g207,g209)
    c: InternalAlignment(g208,g209)
    c: InternalAlignment(g210,g209)
    c: InternalAlignment(g211,g209)
    c: Weight(g212) = 1
    c: Equal(g212,g213)
    c: Equal(g212,g214)
    c: InternalAlignment(g212,g215)
    c: InternalAlignment(g213,g215)
    c: InternalAlignment(g214,g215)
    c: InternalAlignment(g216,g215)
    c: InternalAlignment(g217,g215)
    c: Block(g215)
    c: Block(g209)
    c: Coincident(g218,g215)
    c: Coincident(g218,g46)
    c: Coincident(g219,g46)
    c: Coincident(g219,g209)
    c: Coincident(g220,g209)
    c: Coincident(g220,g215)
    c: Vertical(g220)
    c: Weight(g221) = 1
    c: Equal(g221,g222)
    c: Equal(g221,g223)
    c: InternalAlignment(g221,g224)
    c: InternalAlignment(g222,g224)
    c: InternalAlignment(g223,g224)
    c: InternalAlignment(g225,g224)
    c: InternalAlignment(g226,g224)
    c: Weight(g227) = 1
    c: Equal(g227,g228)
    c: Equal(g227,g229)
    c: InternalAlignment(g227,g230)
    c: InternalAlignment(g228,g230)
    c: InternalAlignment(g229,g230)
    c: InternalAlignment(g231,g230)
    c: InternalAlignment(g232,g230)
    c: Block(g230)
    c: Block(g224)
    c: Coincident(g233,g224)
    c: Coincident(g233,g52)
    c: Coincident(g234,g52)
    c: Coincident(g234,g230)
    c: Coincident(g235,g230)
    c: Coincident(g235,g224)
    c: Vertical(g235)
    c: Horizontal(g236)
    c: Block(g236)
    c: Vertical(g237)
    c: Block(g237)
    c: Block(g238)
    c: Weight(g239) = 1
    c: Equal(g239,g240)
    c: Equal(g239,g241)
    c: InternalAlignment(g239,g242)
    c: InternalAlignment(g240,g242)
    c: InternalAlignment(g241,g242)
    c: InternalAlignment(g243,g242)
    c: InternalAlignment(g244,g242)
    c: Weight(g245) = 1
    c: Equal(g245,g246)
    c: Equal(g245,g247)
    c: InternalAlignment(g245,g248)
    c: InternalAlignment(g246,g248)
    c: InternalAlignment(g247,g248)
    c: InternalAlignment(g249,g248)
    c: InternalAlignment(g250,g248)
    c: Weight(g251) = 1
    c: Equal(g251,g252)
    c: Equal(g251,g253)
    c: InternalAlignment(g251,g254)
    c: InternalAlignment(g252,g254)
    c: InternalAlignment(g253,g254)
    c: InternalAlignment(g255,g254)
    c: InternalAlignment(g256,g254)
    c: Weight(g257) = 1
    c: Equal(g257,g258)
    c: Equal(g257,g259)
    c: InternalAlignment(g257,g260)
    c: InternalAlignment(g258,g260)
    c: InternalAlignment(g259,g260)
    c: InternalAlignment(g261,g260)
    c: InternalAlignment(g262,g260)
    c: Block(g242)
    c: Block(g248)
    c: Block(g254)
    c: Block(g260)
    c: Coincident(g263,g248)
    c: Coincident(g263,g242)
    c: Horizontal(g263)
    c: Block(g205)
    c: Weight(g264) = 1
    c: Equal(g264,g265)
    c: Equal(g264,g266)
    c: InternalAlignment(g264,g267)
    c: InternalAlignment(g265,g267)
    c: InternalAlignment(g266,g267)
    c: InternalAlignment(g268,g267)
    c: InternalAlignment(g269,g267)
    c: Weight(g270) = 1
    c: Equal(g270,g271)
    c: Equal(g270,g272)
    c: InternalAlignment(g270,g273)
    c: InternalAlignment(g271,g273)
    c: InternalAlignment(g272,g273)
    c: InternalAlignment(g274,g273)
    c: InternalAlignment(g275,g273)
    c: Weight(g276) = 1
    c: Equal(g276,g277)
    c: Equal(g276,g278)
    c: InternalAlignment(g276,g279)
    c: InternalAlignment(g277,g279)
    c: InternalAlignment(g278,g279)
    c: InternalAlignment(g280,g279)
    c: InternalAlignment(g281,g279)
    c: Weight(g282) = 1
    c: Equal(g282,g283)
    c: Equal(g282,g284)
    c: InternalAlignment(g282,g285)
    c: InternalAlignment(g283,g285)
    c: InternalAlignment(g284,g285)
    c: InternalAlignment(g286,g285)
    c: InternalAlignment(g287,g285)
    c: Block(g267)
    c: Block(g273)
    c: Block(g279)
    c: Block(g285)
    c: Coincident(g288,g279)
    c: Coincident(g288,g285)
    c: Horizontal(g288)
    c: Coincident(g289,g285)
    c: Coincident(g289,g267)
    c: Vertical(g289)
    c: Coincident(g290,g267)
    c: Coincident(g290,g273)
    c: Coincident(g291,g273)
    c: Coincident(g291,g279)
    c: Vertical(g291)
    c: Horizontal(g294)
    c: Horizontal(g295)
    c: Vertical(g296)
    c: Vertical(g297)
    c: Parallel(g292,g1)
    c: Parallel(g293,g1)
    c: Distance(g297) = 4
    c: Distance(g292) = 4
    c: Distance(g296) = 4
    c: Distance(g295) = 4
    c: Distance(g294) = 4
    c: Distance(g293) = 4
FEATURE [Sketcher::SketchObject] Sketch001
  FullyConstrained = true
  MapMode = 4
  Placement = pos=(0,0,0) rot=(0.57735,0.57735,0.57735;2.0944rad)
  Support = -> [Sketch]
  sketch-geometry (46):
    g0: BSplineCurve PolesCount=3 KnotsCount=2 Degree=2 IsPeriodic=0
    g1: ArcOfCircle CenterX=73.1223 CenterY=-32.291 CenterZ=0 NormalX=0 NormalY=0 NormalZ=1 AngleXU=0 Radius=13 StartAngle=5.92268 EndAngle=9.06428
    g2: ArcOfCircle CenterX=66.7816 CenterY=-49.1439 CenterZ=0 NormalX=0 NormalY=0 NormalZ=1 AngleXU=0 Radius=13 StartAngle=2.78068 EndAngle=5.92131
    g3: ArcOfCircle CenterX=55.9263 CenterY=-78.1807 CenterZ=0 NormalX=0 NormalY=0 NormalZ=1 AngleXU=0 Radius=13 StartAngle=5.92268 EndAngle=9.06428
    g4: ArcOfCircle CenterX=49.5884 CenterY=-95.0342 CenterZ=0 NormalX=0 NormalY=0 NormalZ=1 AngleXU=0 Radius=13 StartAngle=2.78068 EndAngle=5.92131
    g5: ArcOfCircle CenterX=38.7206 CenterY=-124.067 CenterZ=0 NormalX=0 NormalY=0 NormalZ=1 AngleXU=0 Radius=13 StartAngle=5.92268 EndAngle=9.06428
    g6: ArcOfCircle CenterX=32.3875 CenterY=-140.92 CenterZ=0 NormalX=0 NormalY=0 NormalZ=1 AngleXU=0 Radius=13 StartAngle=2.78068 EndAngle=5.92131
    g7: ArcOfCircle CenterX=21.4715 CenterY=-169.934 CenterZ=0 NormalX=0 NormalY=0 NormalZ=1 AngleXU=0 Radius=13 StartAngle=5.92268 EndAngle=9.06428
    g8: ArcOfCircle CenterX=15.1336 CenterY=-186.787 CenterZ=0 NormalX=0 NormalY=0 NormalZ=1 AngleXU=0 Radius=13 StartAngle=2.78068 EndAngle=5.92131
    g9-g12: Circle x4 (B-spline internal-alignment scaffolding for g13; pole/knot coordinates omitted)
    g13: BSplineCurve PolesCount=4 KnotsCount=2 Degree=3 IsPeriodic=0
    g14: GeomPoint X=28.8094 Y=-19.0875 Z=0
    g15: GeomPoint X=47.0443 Y=-50.4712 Z=0
    g16: Circle CenterX=53.5586 CenterY=-23.2695 CenterZ=0 NormalX=0 NormalY=0 NormalZ=1 AngleXU=0 Radius=3.24518
    g17: Circle CenterX=-195.441 CenterY=-127.082 CenterZ=0 NormalX=0 NormalY=0 NormalZ=1 AngleXU=0 Radius=1
    g18: Circle CenterX=-8.24091 CenterY=-197.481 CenterZ=0 NormalX=0 NormalY=0 NormalZ=1 AngleXU=0 Radius=1
    g19: Circle CenterX=12.8789 CenterY=-141.321 CenterZ=0 NormalX=0 NormalY=0 NormalZ=1 AngleXU=0 Radius=1
    g20: BSplineCurve PolesCount=3 KnotsCount=2 Degree=2 IsPeriodic=0
    g21: GeomPoint X=-195.441 Y=-127.082 Z=0
    g22: GeomPoint X=12.8789 Y=-141.321 Z=0
    g23: Circle CenterX=-12.8016 CenterY=-179.036 CenterZ=0 NormalX=0 NormalY=0 NormalZ=1 AngleXU=0 Radius=10.5072
    g24: Circle CenterX=0.933922 CenterY=-166.43 CenterZ=0 NormalX=0 NormalY=0 NormalZ=1 AngleXU=0 Radius=3.26661
    g25: Circle CenterX=-33.5518 CenterY=-176.44 CenterZ=0 NormalX=0 NormalY=0 NormalZ=1 AngleXU=0 Radius=5.64388
    g26: Circle CenterX=-47.2366 CenterY=-173.859 CenterZ=0 NormalX=0 NormalY=0 NormalZ=1 AngleXU=0 Radius=3.01653
    g27: Circle CenterX=-56.2595 CenterY=-171.456 CenterZ=0 NormalX=0 NormalY=0 NormalZ=1 AngleXU=0 Radius=2.12826
    g28: ArcOfCircle CenterX=51.2151 CenterY=-198.473 CenterZ=0 NormalX=0 NormalY=0 NormalZ=1 AngleXU=0 Radius=20 StartAngle=2.78189 EndAngle=4.35269
    g29: LineSegment StartX=32.4951 StartY=-191.433 StartZ=0 EndX=94.6578 EndY=-26.1352 EndZ=0
    g30: LineSegment StartX=43.1192 StartY=-220.001 StartZ=0 EndX=-196.497 EndY=-129.89 EndZ=0
    g31: LineSegment StartX=43.1192 StartY=-220.001 StartZ=0 EndX=44.1752 EndY=-217.193 EndZ=0
    g32: LineSegment StartX=117.223 StartY=-19.0875 StartZ=0 EndX=117.223 EndY=-16.0875 EndZ=0
    g33: LineSegment StartX=117.223 StartY=-16.0875 StartZ=0 EndX=17.2232 EndY=-16.0875 EndZ=0
    g34: LineSegment StartX=17.2232 StartY=-16.0875 StartZ=0 EndX=17.2232 EndY=-19.0875 EndZ=0
    g35: LineSegment StartX=28.8094 StartY=-19.0875 StartZ=0 EndX=17.2232 EndY=-19.0875 EndZ=0
    g36: LineSegment StartX=47.0443 StartY=-50.4712 StartZ=0 EndX=12.8789 EndY=-141.321 EndZ=0
    g37: LineSegment StartX=-195.441 StartY=-127.082 StartZ=0 EndX=-196.497 EndY=-129.89 EndZ=0
    g38: LineSegment StartX=85.2866 StartY=-36.8766 StartZ=0 EndX=78.9396 EndY=-53.7463 EndZ=0
    g39: LineSegment StartX=60.9579 StartY=-27.7053 StartZ=0 EndX=54.6191 EndY=-44.5532 EndZ=0
    g40: LineSegment StartX=68.0907 StartY=-82.7664 StartZ=0 EndX=61.7465 EndY=-99.6365 EndZ=0
    g41: LineSegment StartX=43.7619 StartY=-73.595 StartZ=0 EndX=37.426 EndY=-90.4435 EndZ=0
    g42: LineSegment StartX=50.885 StartY=-128.652 StartZ=0 EndX=44.5456 EndY=-145.522 EndZ=0
    g43: LineSegment StartX=26.5562 StartY=-119.481 StartZ=0 EndX=20.2251 EndY=-136.329 EndZ=0
    g44: LineSegment StartX=9.3071 StartY=-165.349 StartZ=0 EndX=2.97115 EndY=-182.197 EndZ=0
    g45: LineSegment StartX=33.6358 StartY=-174.52 StartZ=0 EndX=27.2917 EndY=-191.39 EndZ=0
  constraints (71):
    c: Block(g0)
    c: Block(g1)
    c: Block(g2)
    c: Block(g4)
    c: Block(g3)
    c: Block(g6)
    c: Block(g5)
    c: Block(g8)
    c: Block(g7)
    c: Weight(g9) = 1
    c: Equal(g9,g10)
    c: Equal(g9,g11)
    c: Equal(g9,g12)
    c: InternalAlignment(g9-g12 -> g13) x4
    c: InternalAlignment(g14,g13)
    c: InternalAlignment(g15,g13)
    c: Block(g16)
    c: Weight(g17) = 1
    c: Equal(g17,g18)
    c: Equal(g17,g19)
    c: InternalAlignment(g17,g20)
    c: InternalAlignment(g18,g20)
    c: InternalAlignment(g19,g20)
    c: InternalAlignment(g21,g20)
    c: InternalAlignment(g22,g20)
    c: Block(g20)
    c: Block(g23)
    c: Block(g24)
    c: Block(g25)
    c: Block(g26)
    c: Block(g27)
    c: Block(g28)
    c: Coincident(g29,g28)
    c: Coincident(g29,g0)
    c: Block(g13)
    c: Coincident(g31,g30)
    c: Coincident(g31,g28)
    c: Block(g31)
    c: Coincident(g32,g0)
    c: Vertical(g32)
    c: Coincident(g33,g32)
    c: Horizontal(g33)
    c: Coincident(g34,g33)
    c: Vertical(g34)
    c: Block(g33)
    c: Coincident(g35,g13)
    c: Coincident(g35,g34)
    c: Horizontal(g35)
    c: Coincident(g36,g13)
    c: Coincident(g36,g20)
    c: Coincident(g37,g20)
    c: Coincident(g37,g30)
    c: Block(g30)
    c: Coincident(g38,g1)
    c: Coincident(g38,g2)
    c: Coincident(g39,g1)
    c: Coincident(g39,g2)
    c: Coincident(g40,g3)
    c: Coincident(g40,g4)
    c: Coincident(g41,g3)
    c: Coincident(g41,g4)
    c: Coincident(g42,g5)
    c: Coincident(g42,g6)
    c: Coincident(g43,g5)
    c: Coincident(g43,g6)
    c: Coincident(g44,g7)
    c: Coincident(g44,g8)
    c: Coincident(g45,g7)
    c: Coincident(g45,g8)
    c: Distance(g30) = 256
    c: Distance(g33) = 100
FEATURE [Part::Extrusion] Extrude002
  Base = -> Sketch001
  Dir = (1,0,0)
  DirMode = 2
  FaceMakerClass = Part::FaceMakerBullseye
  LengthFwd = 8
  LengthRev = 0
  Solid = true
  Symmetric = false
FEATURE [Sketcher::SketchObject] Sketch002
  FullyConstrained = true
  sketch-geometry (20):
    g0: LineSegment StartX=-2.77179 StartY=-200.304 StartZ=0 EndX=5.22821 EndY=-200.304 EndZ=0
    g1: LineSegment StartX=5.22821 StartY=-200.304 StartZ=0 EndX=5.22821 EndY=-197.304 EndZ=0
    g2: LineSegment StartX=-2.77179 StartY=-200.304 StartZ=0 EndX=-2.77179 EndY=-197.304 EndZ=0
    g3: LineSegment StartX=5.22821 StartY=-197.304 StartZ=0 EndX=8.22821 EndY=-197.304 EndZ=0
    g4: LineSegment StartX=-2.77179 StartY=-197.304 StartZ=0 EndX=-5.77179 EndY=-197.304 EndZ=0
    g5: LineSegment StartX=19.2282 StartY=-203.304 StartZ=0 EndX=19.2282 EndY=-206.304 EndZ=0
    g6: LineSegment StartX=-16.7718 StartY=-203.304 StartZ=0 EndX=-16.7718 EndY=-206.304 EndZ=0
    g7: LineSegment StartX=-16.7718 StartY=-206.304 StartZ=0 EndX=19.2282 EndY=-206.304 EndZ=0
    g8: Circle CenterX=-16.7718 CenterY=-203.304 CenterZ=0 NormalX=0 NormalY=0 NormalZ=1 AngleXU=0 Radius=1
    g9: Circle CenterX=-5.77179 CenterY=-203.304 CenterZ=0 NormalX=0 NormalY=0 NormalZ=1 AngleXU=0 Radius=1
    g10: Circle CenterX=-5.77179 CenterY=-197.304 CenterZ=0 NormalX=0 NormalY=0 NormalZ=1 AngleXU=0 Radius=1
    g11: BSplineCurve PolesCount=3 KnotsCount=2 Degree=2 IsPeriodic=0
    g12: GeomPoint X=-16.7718 Y=-203.304 Z=0
    g13: GeomPoint X=-5.77179 Y=-197.304 Z=0
    g14: Circle CenterX=19.2282 CenterY=-203.304 CenterZ=0 NormalX=0 NormalY=0 NormalZ=1 AngleXU=0 Radius=1
    g15: Circle CenterX=8.22821 CenterY=-203.304 CenterZ=0 NormalX=0 NormalY=0 NormalZ=1 AngleXU=0 Radius=1
    g16: Circle CenterX=8.22821 CenterY=-197.304 CenterZ=0 NormalX=0 NormalY=0 NormalZ=1 AngleXU=0 Radius=1
    g17: BSplineCurve PolesCount=3 KnotsCount=2 Degree=2 IsPeriodic=0
    g18: GeomPoint X=19.2282 Y=-203.304 Z=0
    g19: GeomPoint X=8.22821 Y=-197.304 Z=0
  constraints (41):
    c: Horizontal(g0)
    c: Distance(g0) = 8
    c: Coincident(g1,g0)
    c: Vertical(g1)
    c: Distance(g1) = 3
    c: Coincident(g2,g0)
    c: Vertical(g2)
    c: Distance(g2) = 3
    c: Coincident(g3,g1)
    c: Horizontal(g3)
    c: Distance(g3) = 3
    c: Coincident(g4,g2)
    c: Horizontal(g4)
    c: Distance(g4) = 3
    c: Vertical(g5)
    c: Vertical(g6)
    c: Coincident(g7,g6)
    c: Coincident(g7,g5)
    c: Weight(g8) = 1
    c: Equal(g8,g9)
    c: Equal(g8,g10)
    c: Coincident(g11,g4)
    c: InternalAlignment(g8,g11)
    c: InternalAlignment(g9,g11)
    c: InternalAlignment(g10,g11)
    c: InternalAlignment(g12,g11)
    c: InternalAlignment(g13,g11)
    c: Coincident(g17,g5)
    c: Weight(g14) = 1
    c: Equal(g14,g15)
    c: Equal(g14,g16)
    c: Coincident(g17,g3)
    c: InternalAlignment(g14,g17)
    c: InternalAlignment(g15,g17)
    c: InternalAlignment(g16,g17)
    c: InternalAlignment(g18,g17)
    c: InternalAlignment(g19,g17)
    c: Block(g7)
    c: Block(g17)
    c: Block(g11)
    c: Block(g6)
FEATURE [Part::Extrusion] Extrude003
  Base = -> Sketch002
  Dir = (0,0,1)
  DirMode = 2
  FaceMakerClass = Part::FaceMakerBullseye
  LengthFwd = 260
  LengthRev = 0
  Solid = true
  Symmetric = false
FEATURE [Part::Extrusion] Extrude
  Base = -> Sketch
  Dir = (0,0,1)
  DirMode = 2
  FaceMakerClass = Part::FaceMakerBullseye
  LengthFwd = 14
  LengthRev = 0
  Solid = true
  Symmetric = false
